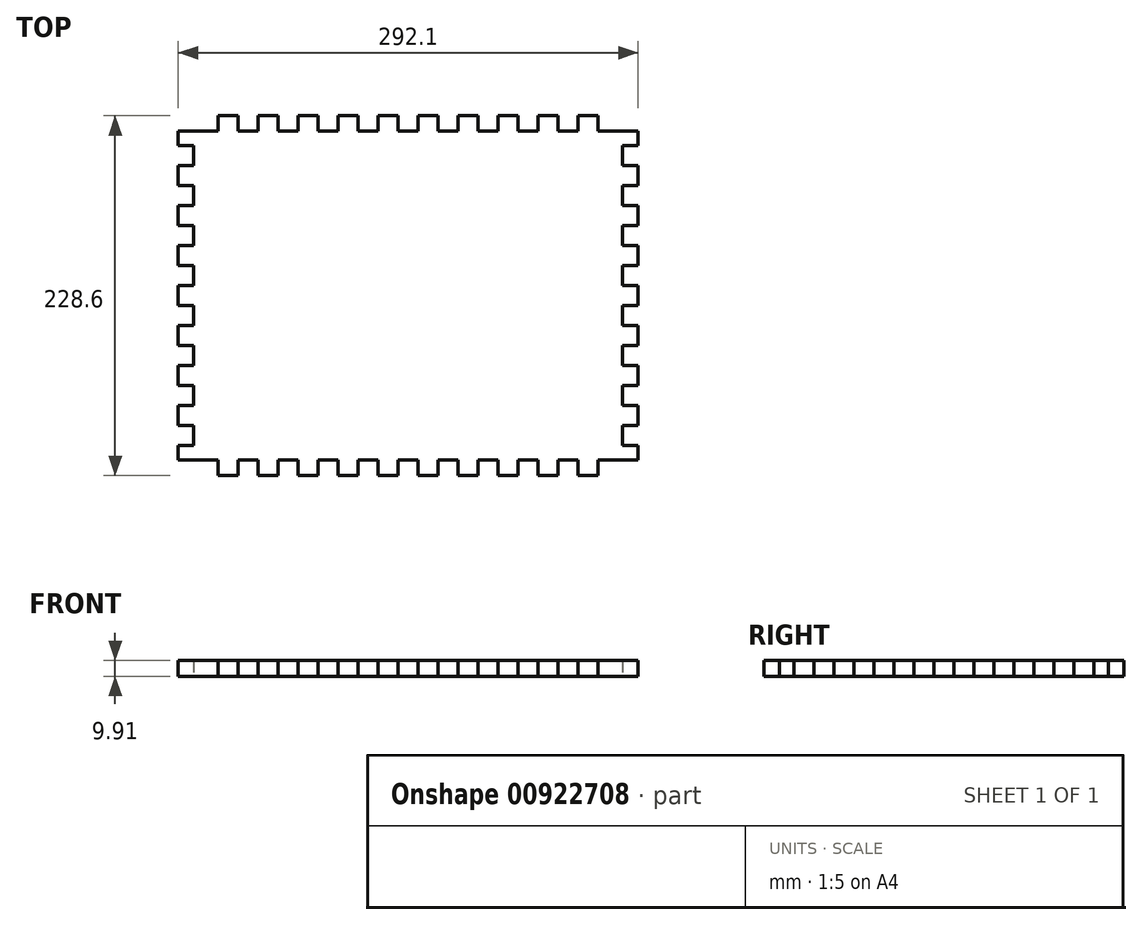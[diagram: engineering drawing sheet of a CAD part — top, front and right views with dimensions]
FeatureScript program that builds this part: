
annotation { "Feature Type Name" : "Feature", "Feature Type Description" : "" }
export const myFeature = defineFeature(function(context is Context, id is Id, definition is map)
    precondition{}
    {
        {
            var Q0;
            Q0=qCreatedBy(makeId("Top.planeOp"),FACE);
            var sketch = newSketch(context, id + "F0", { "sketchPlane" : qUnion([Q0])});
            skLineSegment(sketch, "E0.bottom", {"start": v(25.4, 0) * mm, "end": v(38.1, 0) * mm});
            skLineSegment(sketch, "E0.left", {"start": v(0, -9.9) * mm, "end": v(0, -19.05) * mm});
            skLineSegment(sketch, "E1", {"start": v(0, -9.9) * mm, "end": v(25.4, -9.9) * mm});
            skLineSegment(sketch, "E2", {"start": v(25.4, -9.9) * mm, "end": v(25.4, 0) * mm});
            skLineSegment(sketch, "E3", {"start": v(38.1, 0) * mm, "end": v(38.1, -9.9) * mm});
            skLineSegment(sketch, "E4", {"start": v(38.1, -9.9) * mm, "end": v(50.8, -9.9) * mm});
            skLineSegment(sketch, "E5", {"start": v(50.8, -9.9) * mm, "end": v(50.8, 0) * mm});
            skLineSegment(sketch, "E6", {"start": v(50.8, 0) * mm, "end": v(63.5, 0) * mm});
            skLineSegment(sketch, "E7", {"start": v(63.5, 0) * mm, "end": v(63.5, -9.9) * mm});
            skLineSegment(sketch, "E8", {"start": v(63.5, -9.9) * mm, "end": v(76.2, -9.9) * mm});
            skLineSegment(sketch, "E9", {"start": v(76.2, -9.9) * mm, "end": v(76.2, 0) * mm});
            skLineSegment(sketch, "E10", {"start": v(76.2, 0) * mm, "end": v(88.9, 0) * mm});
            skLineSegment(sketch, "E11", {"start": v(88.9, 0) * mm, "end": v(88.9, -9.9) * mm});
            skLineSegment(sketch, "E12", {"start": v(88.9, -9.9) * mm, "end": v(101.6, -9.9) * mm});
            skLineSegment(sketch, "E13", {"start": v(101.6, -9.9) * mm, "end": v(101.6, 0) * mm});
            skPoint(sketch, "E14.orphan", {"position": v(0, 0) * mm});
            skLineSegment(sketch, "E15.trimOffspring", {"start": v(101.6, 0) * mm, "end": v(114.3, 0) * mm});
            skLineSegment(sketch, "E16", {"start": v(114.3, 0) * mm, "end": v(114.3, -9.9) * mm});
            skLineSegment(sketch, "E17", {"start": v(114.3, -9.9) * mm, "end": v(127, -9.9) * mm});
            skLineSegment(sketch, "E18", {"start": v(127, -9.9) * mm, "end": v(127, 0) * mm});
            skLineSegment(sketch, "E19", {"start": v(127, 0) * mm, "end": v(139.7, 0) * mm});
            skLineSegment(sketch, "E20", {"start": v(139.7, 0) * mm, "end": v(139.7, -9.9) * mm});
            skLineSegment(sketch, "E21", {"start": v(139.7, -9.9) * mm, "end": v(152.4, -9.9) * mm});
            skLineSegment(sketch, "E22", {"start": v(152.4, -9.9) * mm, "end": v(152.4, 0) * mm});
            skLineSegment(sketch, "E23", {"start": v(152.4, 0) * mm, "end": v(165.1, 0) * mm});
            skLineSegment(sketch, "E24", {"start": v(165.1, 0) * mm, "end": v(165.1, -9.9) * mm});
            skLineSegment(sketch, "E25", {"start": v(165.1, -9.9) * mm, "end": v(177.8, -9.9) * mm});
            skLineSegment(sketch, "E26", {"start": v(177.8, -9.9) * mm, "end": v(177.8, 0) * mm});
            skLineSegment(sketch, "E27", {"start": v(177.8, 0) * mm, "end": v(190.5, 0) * mm});
            skLineSegment(sketch, "E28", {"start": v(190.5, 0) * mm, "end": v(190.5, -9.9) * mm});
            skLineSegment(sketch, "E29", {"start": v(190.5, -9.9) * mm, "end": v(203.2, -9.9) * mm});
            skLineSegment(sketch, "E30", {"start": v(203.2, -9.9) * mm, "end": v(203.2, 0) * mm});
            skLineSegment(sketch, "E31.trimOffspring", {"start": v(203.2, 0) * mm, "end": v(215.9, 0) * mm});
            skLineSegment(sketch, "E32", {"start": v(215.9, 0) * mm, "end": v(215.9, -9.9) * mm});
            skLineSegment(sketch, "E33", {"start": v(215.9, -9.9) * mm, "end": v(228.6, -9.9) * mm});
            skLineSegment(sketch, "E34", {"start": v(228.6, -9.9) * mm, "end": v(228.6, 0) * mm});
            skLineSegment(sketch, "E35", {"start": v(228.6, 0) * mm, "end": v(241.3, 0) * mm});
            skLineSegment(sketch, "E36", {"start": v(241.3, 0) * mm, "end": v(241.3, -9.9) * mm});
            skLineSegment(sketch, "E37", {"start": v(241.3, -9.9) * mm, "end": v(254, -9.9) * mm});
            skLineSegment(sketch, "E38", {"start": v(254, -9.9) * mm, "end": v(254, 0) * mm});
            skLineSegment(sketch, "E39.trimOffspring", {"start": v(254, 0) * mm, "end": v(266.7, 0) * mm});
            skLineSegment(sketch, "E40", {"start": v(266.7, 0) * mm, "end": v(266.7, -9.9) * mm});
            skLineSegment(sketch, "E41", {"start": v(266.7, -9.9) * mm, "end": v(292.1, -9.9) * mm});
            skPoint(sketch, "E42.orphan", {"position": v(292.1, 0) * mm});
            skLineSegment(sketch, "E43", {"start": v(0, -19.05) * mm, "end": v(9.9, -19.05) * mm});
            skLineSegment(sketch, "E44", {"start": v(9.9, -19.05) * mm, "end": v(9.9, -31.75) * mm});
            skLineSegment(sketch, "E45", {"start": v(9.9, -31.75) * mm, "end": v(0, -31.75) * mm});
            skLineSegment(sketch, "E46", {"start": v(0, -31.75) * mm, "end": v(0, -44.45) * mm});
            skLineSegment(sketch, "E47", {"start": v(0, -44.45) * mm, "end": v(9.9, -44.45) * mm});
            skLineSegment(sketch, "E48", {"start": v(9.9, -44.45) * mm, "end": v(9.9, -57.15) * mm});
            skLineSegment(sketch, "E49", {"start": v(9.9, -57.15) * mm, "end": v(0, -57.15) * mm});
            skLineSegment(sketch, "E50.trimOffspring", {"start": v(0, -57.15) * mm, "end": v(0, -69.85) * mm});
            skLineSegment(sketch, "E51", {"start": v(0, -69.85) * mm, "end": v(9.9, -69.85) * mm});
            skLineSegment(sketch, "E52", {"start": v(9.9, -69.85) * mm, "end": v(9.9, -82.55) * mm});
            skLineSegment(sketch, "E53", {"start": v(9.9, -82.55) * mm, "end": v(0, -82.55) * mm});
            skLineSegment(sketch, "E54", {"start": v(0, -82.55) * mm, "end": v(0, -95.25) * mm});
            skLineSegment(sketch, "E55", {"start": v(0, -95.25) * mm, "end": v(9.9, -95.25) * mm});
            skLineSegment(sketch, "E56", {"start": v(9.9, -95.25) * mm, "end": v(9.9, -107.95) * mm});
            skLineSegment(sketch, "E57", {"start": v(9.9, -107.95) * mm, "end": v(0, -107.95) * mm});
            skLineSegment(sketch, "E58", {"start": v(0, -107.95) * mm, "end": v(0, -120.65) * mm});
            skLineSegment(sketch, "E59", {"start": v(0, -120.65) * mm, "end": v(9.9, -120.65) * mm});
            skLineSegment(sketch, "E60", {"start": v(9.9, -120.65) * mm, "end": v(9.9, -133.35) * mm});
            skLineSegment(sketch, "E61", {"start": v(9.9, -133.35) * mm, "end": v(0, -133.35) * mm});
            skLineSegment(sketch, "E62.trimOffspring", {"start": v(0, -133.35) * mm, "end": v(0, -146.05) * mm});
            skLineSegment(sketch, "E63", {"start": v(0, -146.05) * mm, "end": v(9.9, -146.05) * mm});
            skLineSegment(sketch, "E64", {"start": v(9.9, -146.05) * mm, "end": v(9.9, -158.75) * mm});
            skLineSegment(sketch, "E65", {"start": v(9.9, -158.75) * mm, "end": v(0, -158.75) * mm});
            skLineSegment(sketch, "E66", {"start": v(0, -158.75) * mm, "end": v(0, -171.45) * mm});
            skLineSegment(sketch, "E67", {"start": v(0, -171.45) * mm, "end": v(9.9, -171.45) * mm});
            skLineSegment(sketch, "E68", {"start": v(9.9, -171.45) * mm, "end": v(9.9, -184.15) * mm});
            skLineSegment(sketch, "E69", {"start": v(9.9, -184.15) * mm, "end": v(0, -184.15) * mm});
            skLineSegment(sketch, "E70.trimOffspring", {"start": v(0, -184.15) * mm, "end": v(0, -196.85) * mm});
            skLineSegment(sketch, "E71", {"start": v(0, -196.85) * mm, "end": v(9.9, -196.85) * mm});
            skLineSegment(sketch, "E72", {"start": v(9.9, -196.85) * mm, "end": v(9.9, -209.55) * mm});
            skLineSegment(sketch, "E73", {"start": v(9.9, -209.55) * mm, "end": v(0, -209.55) * mm});
            skLineSegment(sketch, "E74.trimOffspring", {"start": v(0, -209.55) * mm, "end": v(0, -218.7) * mm});
            skLineSegment(sketch, "E75", {"start": v(0, -218.7) * mm, "end": v(25.4, -218.7) * mm});
            skLineSegment(sketch, "E76", {"start": v(25.4, -218.7) * mm, "end": v(25.4, -218.7) * mm});
            skPoint(sketch, "E77.orphan", {"position": v(0, -228.6) * mm});
            skLineSegment(sketch, "E78", {"start": v(146.05, -9.9) * mm, "end": v(146.05, -9.9) * mm});
            skLineSegment(sketch, "E79", {"start": v(0, -114.3) * mm, "end": v(0, -114.3) * mm});
            skLineSegment(sketch, "E80.MirrorCS", {"start": v(292.1, -31.75) * mm, "end": v(292.1, -44.45) * mm});
            skLineSegment(sketch, "E81.MirrorCS", {"start": v(292.1, -107.95) * mm, "end": v(292.1, -120.65) * mm});
            skLineSegment(sketch, "E82.MirrorCS", {"start": v(292.1, -57.15) * mm, "end": v(292.1, -69.85) * mm});
            skLineSegment(sketch, "E83.MirrorCS", {"start": v(292.1, -184.15) * mm, "end": v(292.1, -196.85) * mm});
            skLineSegment(sketch, "E84.MirrorCS", {"start": v(292.1, -158.75) * mm, "end": v(292.1, -171.45) * mm});
            skLineSegment(sketch, "E85.MirrorCS", {"start": v(292.1, -9.9) * mm, "end": v(292.1, -19.05) * mm});
            skLineSegment(sketch, "E86.MirrorCS", {"start": v(292.1, -133.35) * mm, "end": v(292.1, -146.05) * mm});
            skLineSegment(sketch, "E87.MirrorCS", {"start": v(292.1, -82.55) * mm, "end": v(292.1, -95.25) * mm});
            skLineSegment(sketch, "E88.MirrorCS", {"start": v(292.1, -209.55) * mm, "end": v(292.1, -218.7) * mm});
            skLineSegment(sketch, "E89.MirrorCS", {"start": v(292.1, -95.25) * mm, "end": v(282.2, -95.25) * mm});
            skLineSegment(sketch, "E90.MirrorCS", {"start": v(282.2, -19.05) * mm, "end": v(282.2, -31.75) * mm});
            skLineSegment(sketch, "E91.MirrorCS", {"start": v(292.1, -120.65) * mm, "end": v(282.2, -120.65) * mm});
            skLineSegment(sketch, "E92.MirrorCS", {"start": v(282.2, -158.75) * mm, "end": v(292.1, -158.75) * mm});
            skLineSegment(sketch, "E93.MirrorCS", {"start": v(282.2, -31.75) * mm, "end": v(292.1, -31.75) * mm});
            skLineSegment(sketch, "E94.MirrorCS", {"start": v(292.1, -196.85) * mm, "end": v(282.2, -196.85) * mm});
            skLineSegment(sketch, "E95.MirrorCS", {"start": v(282.2, -184.15) * mm, "end": v(292.1, -184.15) * mm});
            skLineSegment(sketch, "E96.MirrorCS", {"start": v(282.2, -196.85) * mm, "end": v(282.2, -209.55) * mm});
            skLineSegment(sketch, "E97.MirrorCS", {"start": v(282.2, -171.45) * mm, "end": v(282.2, -184.15) * mm});
            skLineSegment(sketch, "E98.MirrorCS", {"start": v(282.2, -107.95) * mm, "end": v(292.1, -107.95) * mm});
            skLineSegment(sketch, "E99.MirrorCS", {"start": v(292.1, -44.45) * mm, "end": v(282.2, -44.45) * mm});
            skLineSegment(sketch, "E100.MirrorCS", {"start": v(282.2, -82.55) * mm, "end": v(292.1, -82.55) * mm});
            skLineSegment(sketch, "E101.MirrorCS", {"start": v(282.2, -57.15) * mm, "end": v(292.1, -57.15) * mm});
            skLineSegment(sketch, "E102.MirrorCS", {"start": v(282.2, -133.35) * mm, "end": v(292.1, -133.35) * mm});
            skLineSegment(sketch, "E103.MirrorCS", {"start": v(292.1, -19.05) * mm, "end": v(282.2, -19.05) * mm});
            skLineSegment(sketch, "E104.MirrorCS", {"start": v(292.1, -171.45) * mm, "end": v(282.2, -171.45) * mm});
            skLineSegment(sketch, "E105.MirrorCS", {"start": v(282.2, -209.55) * mm, "end": v(292.1, -209.55) * mm});
            skLineSegment(sketch, "E106.MirrorCS", {"start": v(292.1, -146.05) * mm, "end": v(282.2, -146.05) * mm});
            skLineSegment(sketch, "E107.MirrorCS", {"start": v(282.2, -95.25) * mm, "end": v(282.2, -107.95) * mm});
            skLineSegment(sketch, "E108.MirrorCS", {"start": v(282.2, -120.65) * mm, "end": v(282.2, -133.35) * mm});
            skLineSegment(sketch, "E109.MirrorCS", {"start": v(282.2, -146.05) * mm, "end": v(282.2, -158.75) * mm});
            skLineSegment(sketch, "E110.MirrorCS", {"start": v(282.2, -69.85) * mm, "end": v(282.2, -82.55) * mm});
            skLineSegment(sketch, "E111.MirrorCS", {"start": v(282.2, -44.45) * mm, "end": v(282.2, -57.15) * mm});
            skLineSegment(sketch, "E112.MirrorCS", {"start": v(292.1, -69.85) * mm, "end": v(282.2, -69.85) * mm});
            skLineSegment(sketch, "E113.MirrorCS", {"start": v(292.1, -218.7) * mm, "end": v(266.7, -218.7) * mm});
            skLineSegment(sketch, "E114.MirrorCS", {"start": v(292.1, -9.9) * mm, "end": v(266.7, -9.9) * mm});
            skLineSegment(sketch, "E115.MirrorCS", {"start": v(292.1, -114.3) * mm, "end": v(292.1, -114.3) * mm});
            skLineSegment(sketch, "E116.MirrorCS", {"start": v(266.7, -218.7) * mm, "end": v(266.7, -218.7) * mm});
            skLineSegment(sketch, "E117.MirrorCS", {"start": v(25.4, -228.6) * mm, "end": v(38.1, -228.6) * mm});
            skLineSegment(sketch, "E118.MirrorCS", {"start": v(127, -228.6) * mm, "end": v(139.7, -228.6) * mm});
            skLineSegment(sketch, "E119.MirrorCS", {"start": v(254, -228.6) * mm, "end": v(266.7, -228.6) * mm});
            skLineSegment(sketch, "E120.MirrorCS", {"start": v(76.2, -228.6) * mm, "end": v(88.9, -228.6) * mm});
            skLineSegment(sketch, "E121.MirrorCS", {"start": v(177.8, -228.6) * mm, "end": v(190.5, -228.6) * mm});
            skLineSegment(sketch, "E122.MirrorCS", {"start": v(152.4, -228.6) * mm, "end": v(165.1, -228.6) * mm});
            skLineSegment(sketch, "E123.MirrorCS", {"start": v(50.8, -228.6) * mm, "end": v(63.5, -228.6) * mm});
            skLineSegment(sketch, "E124.MirrorCS", {"start": v(101.6, -228.6) * mm, "end": v(114.3, -228.6) * mm});
            skLineSegment(sketch, "E125.MirrorCS", {"start": v(203.2, -228.6) * mm, "end": v(215.9, -228.6) * mm});
            skLineSegment(sketch, "E126.MirrorCS", {"start": v(228.6, -228.6) * mm, "end": v(241.3, -228.6) * mm});
            skLineSegment(sketch, "E127.MirrorCS", {"start": v(266.7, -228.6) * mm, "end": v(266.7, -218.7) * mm});
            skLineSegment(sketch, "E128.MirrorCS", {"start": v(190.5, -228.6) * mm, "end": v(190.5, -218.7) * mm});
            skLineSegment(sketch, "E129.MirrorCS", {"start": v(228.6, -218.7) * mm, "end": v(228.6, -228.6) * mm});
            skLineSegment(sketch, "E130.MirrorCS", {"start": v(152.4, -218.7) * mm, "end": v(152.4, -228.6) * mm});
            skLineSegment(sketch, "E131.MirrorCS", {"start": v(139.7, -228.6) * mm, "end": v(139.7, -218.7) * mm});
            skLineSegment(sketch, "E132.MirrorCS", {"start": v(127, -218.7) * mm, "end": v(127, -228.6) * mm});
            skLineSegment(sketch, "E133.MirrorCS", {"start": v(25.4, -218.7) * mm, "end": v(25.4, -228.6) * mm});
            skLineSegment(sketch, "E134.MirrorCS", {"start": v(190.5, -218.7) * mm, "end": v(203.2, -218.7) * mm});
            skLineSegment(sketch, "E135.MirrorCS", {"start": v(38.1, -228.6) * mm, "end": v(38.1, -218.7) * mm});
            skLineSegment(sketch, "E136.MirrorCS", {"start": v(165.1, -228.6) * mm, "end": v(165.1, -218.7) * mm});
            skLineSegment(sketch, "E137.MirrorCS", {"start": v(241.3, -228.6) * mm, "end": v(241.3, -218.7) * mm});
            skLineSegment(sketch, "E138.MirrorCS", {"start": v(203.2, -218.7) * mm, "end": v(203.2, -228.6) * mm});
            skLineSegment(sketch, "E139.MirrorCS", {"start": v(50.8, -218.7) * mm, "end": v(50.8, -228.6) * mm});
            skLineSegment(sketch, "E140.MirrorCS", {"start": v(241.3, -218.7) * mm, "end": v(254, -218.7) * mm});
            skLineSegment(sketch, "E141.MirrorCS", {"start": v(76.2, -218.7) * mm, "end": v(76.2, -228.6) * mm});
            skLineSegment(sketch, "E142.MirrorCS", {"start": v(88.9, -228.6) * mm, "end": v(88.9, -218.7) * mm});
            skLineSegment(sketch, "E143.MirrorCS", {"start": v(139.7, -218.7) * mm, "end": v(152.4, -218.7) * mm});
            skLineSegment(sketch, "E144.MirrorCS", {"start": v(215.9, -228.6) * mm, "end": v(215.9, -218.7) * mm});
            skLineSegment(sketch, "E145.MirrorCS", {"start": v(215.9, -218.7) * mm, "end": v(228.6, -218.7) * mm});
            skLineSegment(sketch, "E146.MirrorCS", {"start": v(88.9, -218.7) * mm, "end": v(101.6, -218.7) * mm});
            skLineSegment(sketch, "E147.MirrorCS", {"start": v(114.3, -218.7) * mm, "end": v(127, -218.7) * mm});
            skLineSegment(sketch, "E148.MirrorCS", {"start": v(114.3, -228.6) * mm, "end": v(114.3, -218.7) * mm});
            skLineSegment(sketch, "E149.MirrorCS", {"start": v(165.1, -218.7) * mm, "end": v(177.8, -218.7) * mm});
            skLineSegment(sketch, "E150.MirrorCS", {"start": v(254, -218.7) * mm, "end": v(254, -228.6) * mm});
            skLineSegment(sketch, "E151.MirrorCS", {"start": v(38.1, -218.7) * mm, "end": v(50.8, -218.7) * mm});
            skLineSegment(sketch, "E152.MirrorCS", {"start": v(63.5, -218.7) * mm, "end": v(76.2, -218.7) * mm});
            skLineSegment(sketch, "E153.MirrorCS", {"start": v(63.5, -228.6) * mm, "end": v(63.5, -218.7) * mm});
            skLineSegment(sketch, "E154.MirrorCS", {"start": v(101.6, -218.7) * mm, "end": v(101.6, -228.6) * mm});
            skLineSegment(sketch, "E155.MirrorCS", {"start": v(177.8, -218.7) * mm, "end": v(177.8, -228.6) * mm});
            skSolve(sketch);
        }
        {
            var Q0;
            Q0=makeQuery(id+"F0.imprint","IMPRINT",FACE,{"disambiguationData":[TD([[makeQuery(id+"F0.imprint","IMPRINT",EDGE,{"derivedFrom":sQuery(id+"F0.wireOp",EDGE,"E1")}),-1.0]])]});
            extrude(context, id + "F1", {"entities" : qUnion([Q0]), "depth" : 9.9 * mm, "offsetDistance" : 25.4 * mm});
        }
    });
